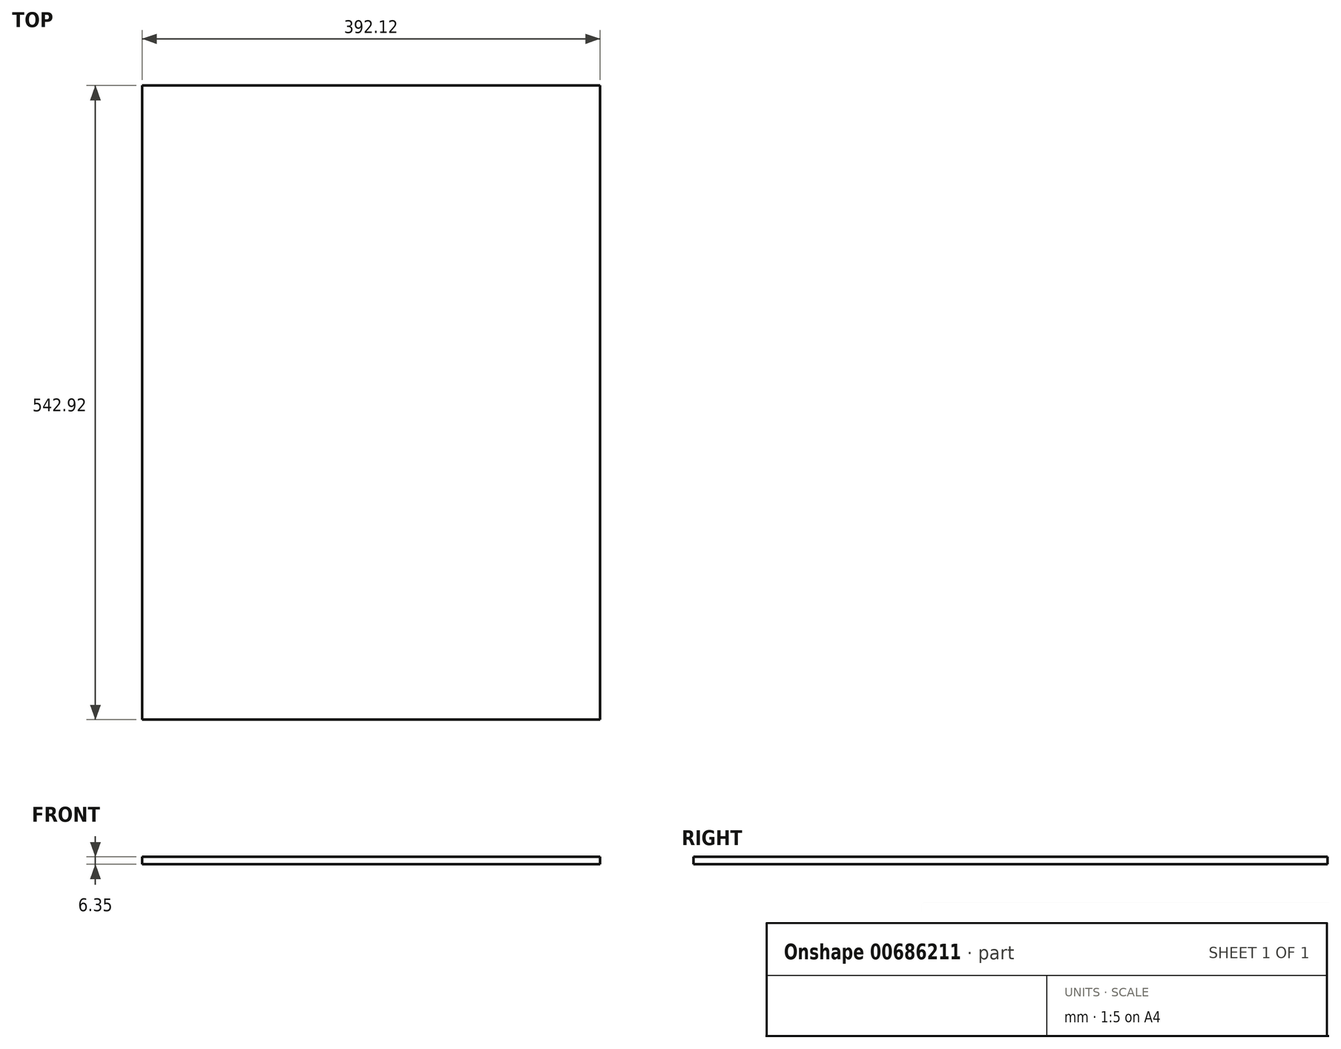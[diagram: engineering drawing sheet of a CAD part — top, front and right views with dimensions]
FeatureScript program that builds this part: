
annotation { "Feature Type Name" : "Feature", "Feature Type Description" : "" }
export const myFeature = defineFeature(function(context is Context, id is Id, definition is map)
    precondition{}
    {
        {
            var Q0;
            Q0=qCreatedBy(makeId("Top.planeOp"),FACE);
            var sketch = newSketch(context, id + "F0", { "sketchPlane" : qUnion([Q0])});
            skLineSegment(sketch, "E0.bottom", {"start": v(-196.06, 271.46) * mm, "end": v(196.06, 271.46) * mm});
            skLineSegment(sketch, "E0.top", {"start": v(-196.06, -271.46) * mm, "end": v(196.06, -271.46) * mm});
            skLineSegment(sketch, "E0.left", {"start": v(-196.06, 271.46) * mm, "end": v(-196.06, -271.46) * mm});
            skLineSegment(sketch, "E0.right", {"start": v(196.06, 271.46) * mm, "end": v(196.06, -271.46) * mm});
            skPoint(sketch, "E0.middle", {"position": v(0, 0) * mm});
            skSolve(sketch);
        }
        {
            var Q0;
            Q0=makeQuery(id+"F0.imprint","IMPRINT",FACE,{"disambiguationData":[TD([[makeQuery(id+"F0.imprint","IMPRINT",EDGE,{"derivedFrom":sQuery(id+"F0.wireOp",EDGE,"E0.bottom")}),-1.0]])]});
            extrude(context, id + "F1", {"entities" : qUnion([Q0]), "depth" : 6.35 * mm, "offsetDistance" : 25.4 * mm});
        }
    });
